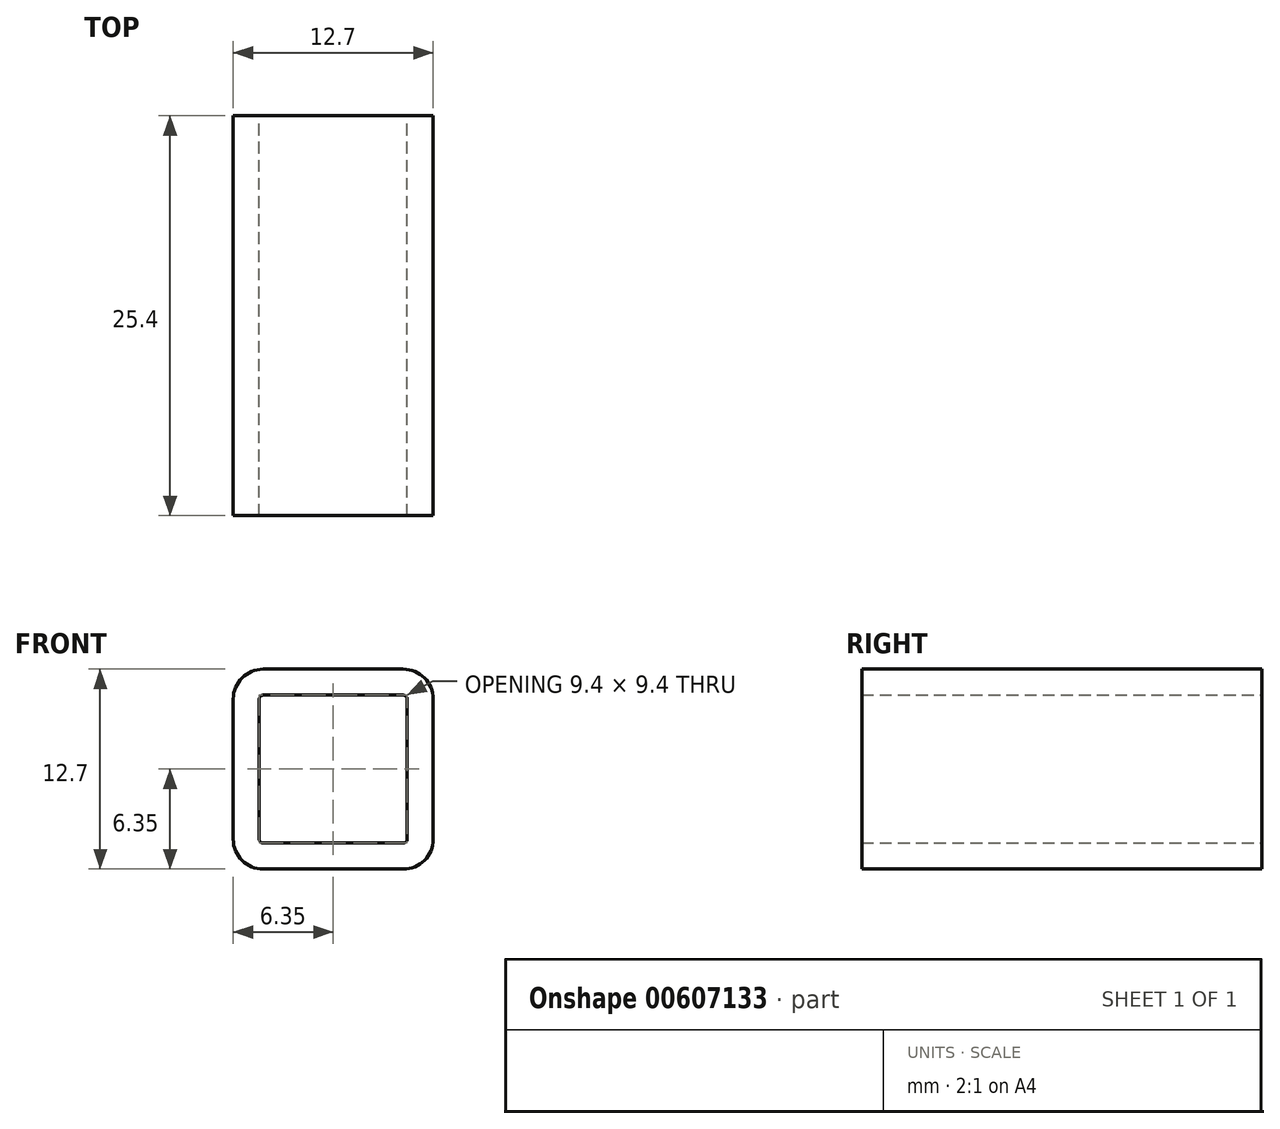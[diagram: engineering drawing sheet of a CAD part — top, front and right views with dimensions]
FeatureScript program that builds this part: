
annotation { "Feature Type Name" : "Feature", "Feature Type Description" : "" }
export const myFeature = defineFeature(function(context is Context, id is Id, definition is map)
    precondition{}
    {
        {
            var Q0;
            Q0=qCreatedBy(makeId("Front.planeOp"),FACE);
            var sketch = newSketch(context, id + "F0", { "sketchPlane" : qUnion([Q0])});
            skLineSegment(sketch, "E0.bottom", {"start": v(4.45, -6.35) * mm, "end": v(-4.45, -6.35) * mm});
            skLineSegment(sketch, "E0.top", {"start": v(4.45, 6.35) * mm, "end": v(-4.45, 6.35) * mm});
            skLineSegment(sketch, "E0.left", {"start": v(6.35, -4.45) * mm, "end": v(6.35, 4.45) * mm});
            skLineSegment(sketch, "E0.right", {"start": v(-6.35, -4.45) * mm, "end": v(-6.35, 4.44) * mm});
            skPoint(sketch, "E0.middle", {"position": v(0, 0) * mm});
            skPoint(sketch, "E1.visualSharp", {"position": v(6.35, 6.35) * mm});
            skArc(sketch, "E1.filletArc", {"start": v(6.35, 4.45) * mm, "mid": v(5.8, 5.8) * mm, "end": v(4.45, 6.35) * mm});
            skPoint(sketch, "E2.visualSharp", {"position": v(6.35, -6.35) * mm});
            skArc(sketch, "E2.filletArc", {"start": v(4.45, -6.35) * mm, "mid": v(5.8, -5.8) * mm, "end": v(6.35, -4.45) * mm});
            skPoint(sketch, "E3.visualSharp", {"position": v(-6.35, -6.35) * mm});
            skArc(sketch, "E3.filletArc", {"start": v(-6.35, -4.45) * mm, "mid": v(-5.8, -5.8) * mm, "end": v(-4.45, -6.35) * mm});
            skPoint(sketch, "E4.visualSharp", {"position": v(-6.35, 6.35) * mm});
            skArc(sketch, "E4.filletArc", {"start": v(-4.45, 6.35) * mm, "mid": v(-5.8, 5.8) * mm, "end": v(-6.35, 4.44) * mm});
            skArc(sketch, "E5.0", {"start": v(4.7, 4.45) * mm, "mid": v(4.62, 4.62) * mm, "end": v(4.45, 4.7) * mm});
            skLineSegment(sketch, "E5.1", {"start": v(4.7, -4.44) * mm, "end": v(4.7, 4.45) * mm});
            skLineSegment(sketch, "E5.2", {"start": v(4.45, 4.7) * mm, "end": v(-4.45, 4.7) * mm});
            skArc(sketch, "E5.3", {"start": v(4.45, -4.7) * mm, "mid": v(4.62, -4.62) * mm, "end": v(4.7, -4.44) * mm});
            skArc(sketch, "E5.4", {"start": v(-4.45, 4.7) * mm, "mid": v(-4.62, 4.62) * mm, "end": v(-4.7, 4.45) * mm});
            skLineSegment(sketch, "E5.5", {"start": v(-4.7, -4.44) * mm, "end": v(-4.7, 4.45) * mm});
            skArc(sketch, "E5.6", {"start": v(-4.7, -4.44) * mm, "mid": v(-4.62, -4.62) * mm, "end": v(-4.45, -4.7) * mm});
            skLineSegment(sketch, "E5.7", {"start": v(4.45, -4.7) * mm, "end": v(-4.45, -4.7) * mm});
            skSolve(sketch);
        }
        {
            var Q0;
            Q0 = qSketchRegion(id + "F0", true);
            extrude(context, id + "F1", {"entities" : qUnion([Q0]), "depth" : 25.4 * mm, "offsetDistance" : 25.4 * mm});
        }
    });
